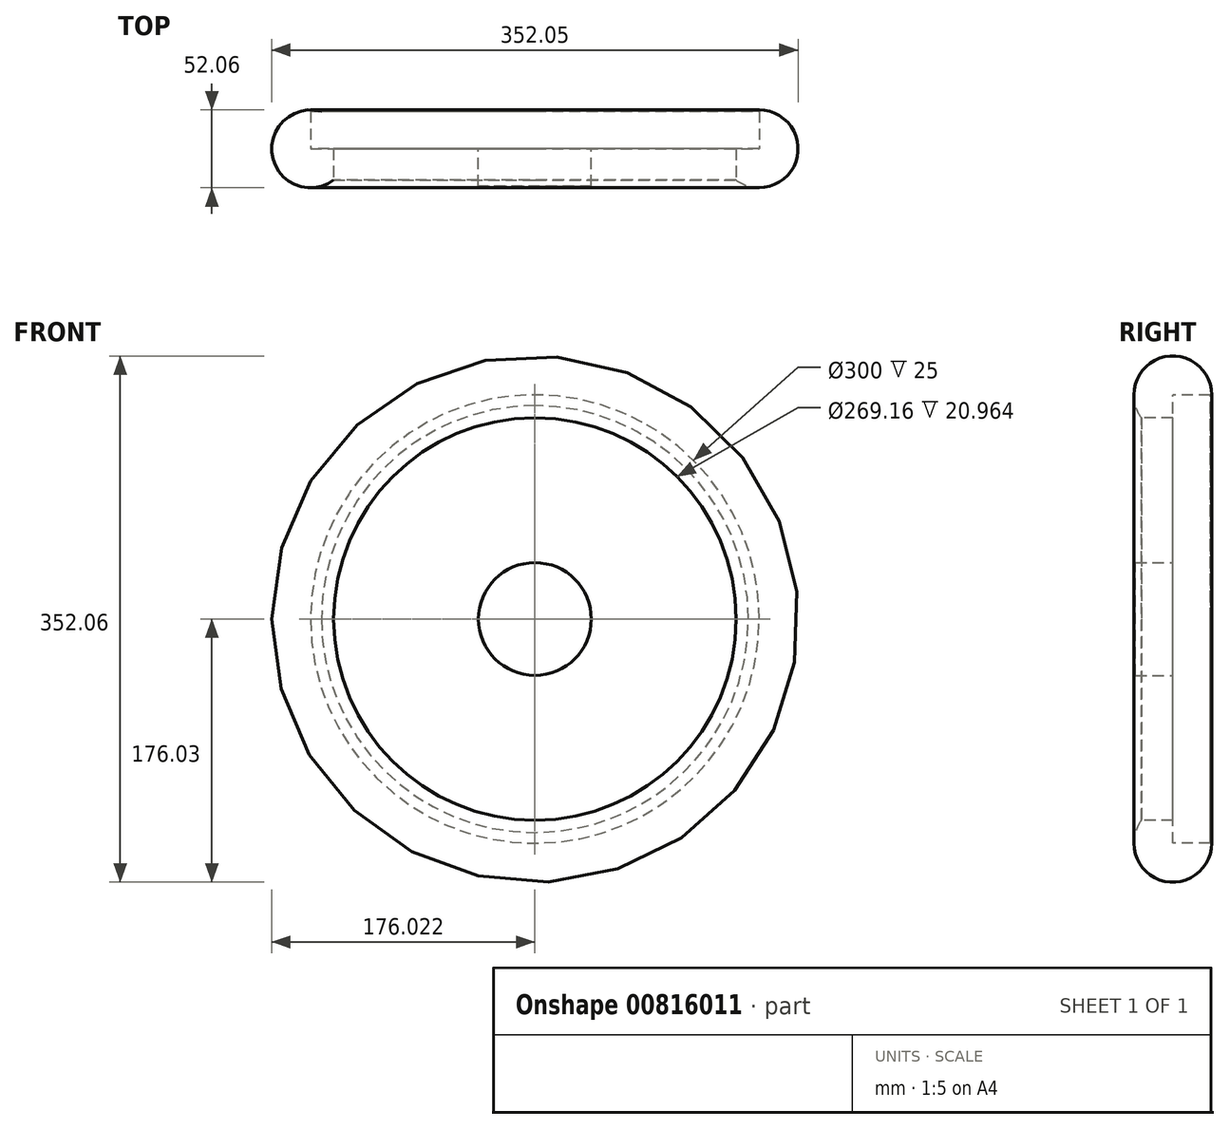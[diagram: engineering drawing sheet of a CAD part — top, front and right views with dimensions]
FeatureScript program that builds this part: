
annotation { "Feature Type Name" : "Feature", "Feature Type Description" : "" }
export const myFeature = defineFeature(function(context is Context, id is Id, definition is map)
    precondition{}
    {
        {
            var Q0;
            Q0=qCreatedBy(makeId("Front.planeOp"),FACE);
            var sketch = newSketch(context, id + "F0", { "sketchPlane" : qUnion([Q0])});
            skArc(sketch, "E0", {"start": v(-53.9, 15.91) * mm, "mid": v(0, -56.2) * mm, "end": v(53.9, 15.91) * mm});
            skPoint(sketch, "E1.middle", {"position": v(0, -22.2) * mm});
            skPoint(sketch, "E1.left.end.orphan", {"position": v(-69.44, 15.91) * mm});
            skPoint(sketch, "E1.bottom.end.orphan", {"position": v(69.44, -60.33) * mm});
            skPoint(sketch, "E1.bottom.start.orphan", {"position": v(-69.44, -60.33) * mm});
            skPoint(sketch, "E1.top.end.orphan", {"position": v(69.44, 15.91) * mm});
            skSolve(sketch);
        }
        {
            var Q0;
            Q0=qCreatedBy(makeId("Top.planeOp"),FACE);
            var sketch = newSketch(context, id + "F1", { "sketchPlane" : qUnion([Q0])});
            skCircle(sketch, "E2", {"center": v(-56.2, 0) * mm, "radius": 9.25 * mm});
            skSolve(sketch);
        }
        {
            var Q0;
            Q0=makeQuery(id+"F1.imprint","IMPRINT",FACE,{"disambiguationData":[TD([[makeQuery(id+"F1.imprint","IMPRINT",EDGE,{"derivedFrom":sQuery(id+"F1.wireOp",EDGE,"E2")}),1.0]])]});
            var Q1;
            Q1=sQuery(id+"F0.wireOp",EDGE,"E0");
            sweep(context, id + "F2", {"profiles" : qUnion([Q0]), "path" : qUnion([Q1])});
        }
        {
            var Q0;
            Q0=makeQuery(id+"F2.opSweep","SWEPT_BODY",BODY,{"disambiguationData":[OSD([sQuery(id+"F0.wireOp",EDGE,"E0"),sQuery(id+"F1.wireOp",EDGE,"E2")])]});
            deleteBodies(context, id + "F3", {"entities" : qUnion([Q0])});
        }
        {
            var Q0;
            Q0=qCreatedBy(makeId("Front.planeOp"),FACE);
            var sketch = newSketch(context, id + "F4", { "sketchPlane" : qUnion([Q0])});
            skCircle(sketch, "E3", {"center": v(-70.7, 0) * mm, "radius": 150 * mm});
            skCircle(sketch, "E4", {"center": v(-70.7, 0) * mm, "radius": 37.73 * mm});
            skSolve(sketch);
        }
        {
            var Q0;
            Q0=qCreatedBy(makeId("Top.planeOp"),FACE);
            var sketch = newSketch(context, id + "F5", { "sketchPlane" : qUnion([Q0])});
            skArc(sketch, "E5", {"start": v(-205.28, 20.96) * mm, "mid": v(-246.72, 0) * mm, "end": v(-205.28, -20.96) * mm});
            skLineSegment(sketch, "E6", {"start": v(-205.28, -20.96) * mm, "end": v(-205.28, 20.96) * mm});
            skSolve(sketch);
        }
        {
            var Q0;
            Q0=makeQuery(id+"F5.imprint","IMPRINT",FACE,{"disambiguationData":[TD([[makeQuery(id+"F5.imprint","IMPRINT",EDGE,{"derivedFrom":sQuery(id+"F5.wireOp",EDGE,"E5")}),1.0]])]});
            var Q1;
            Q1=sQuery(id+"F4.wireOp",EDGE,"E3");
            sweep(context, id + "F6", {"profiles" : qUnion([Q0]), "path" : qUnion([Q1])});
        }
        {
            var Q0;
            Q0 = qSketchRegion(id + "F4", true);
            extrude(context, id + "F7", {"entities" : qUnion([Q0]), "operationType" : NewBodyOperationType.REMOVE, "oppositeDirection" : true, "depth" : 25 * mm, "offsetDistance" : 25 * mm});
        }
        {
            var Q0;
            Q0=makeQuery(id+"F4.imprint","IMPRINT",FACE,{"disambiguationData":[TD([[makeQuery(id+"F4.imprint","IMPRINT",EDGE,{"derivedFrom":sQuery(id+"F4.wireOp",EDGE,"E4")}),1.0]])]});
            extrude(context, id + "F8", {"entities" : qUnion([Q0]), "depth" : 25 * mm, "offsetDistance" : 25 * mm});
        }
    });
